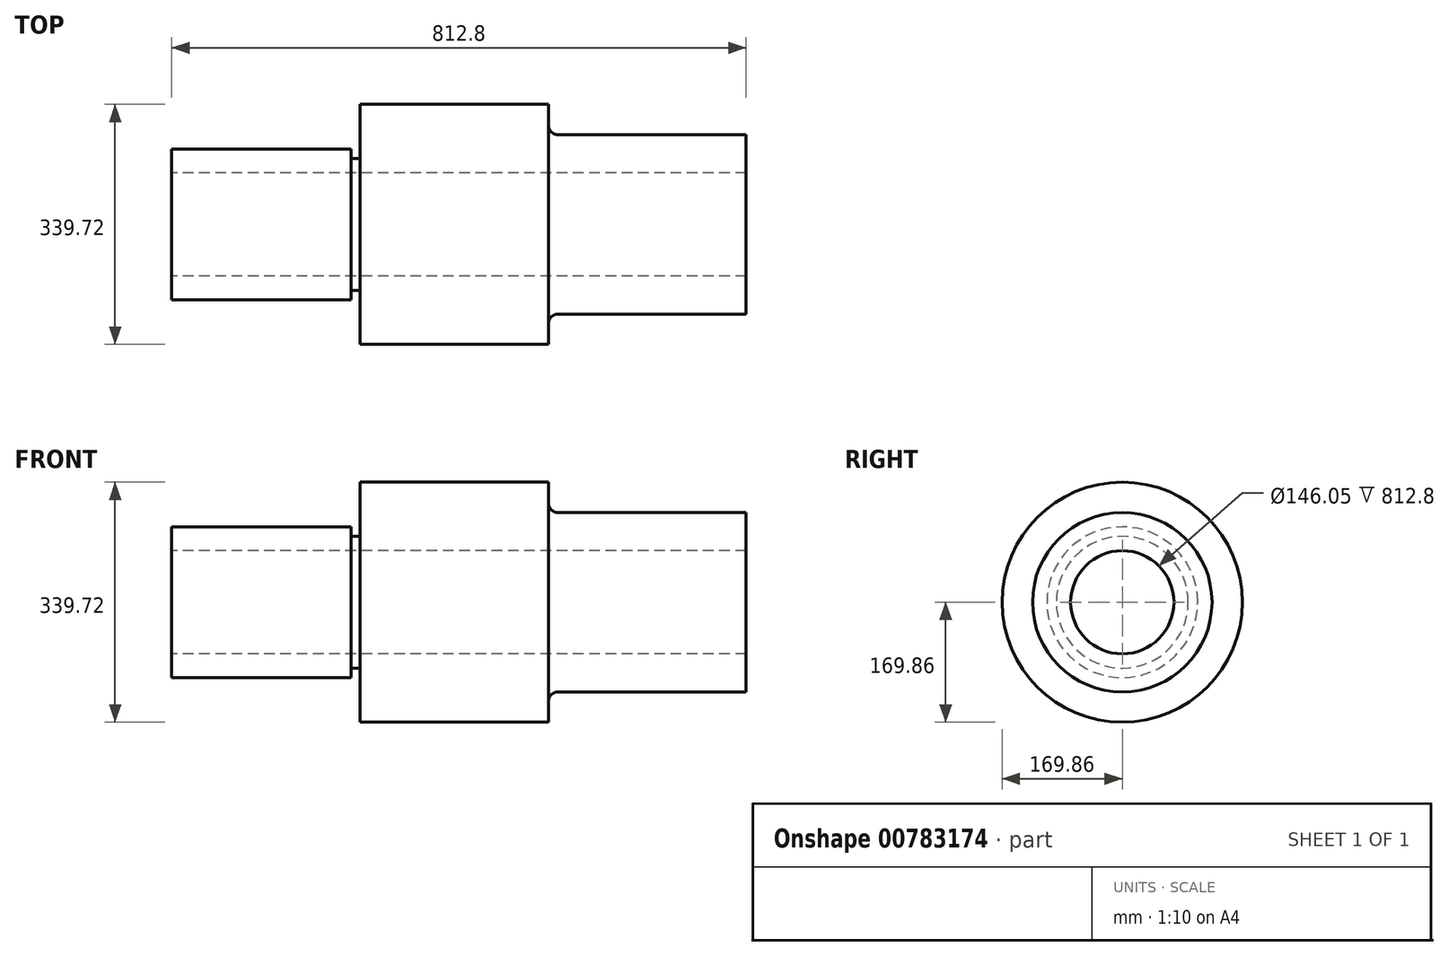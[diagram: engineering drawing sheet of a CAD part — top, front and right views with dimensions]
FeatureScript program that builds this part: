
annotation { "Feature Type Name" : "Feature", "Feature Type Description" : "" }
export const myFeature = defineFeature(function(context is Context, id is Id, definition is map)
    precondition{}
    {
        {
            var Q0;
            Q0=qCreatedBy(makeId("Front.planeOp"),FACE);
            var sketch = newSketch(context, id + "F0", { "sketchPlane" : qUnion([Q0])});
            skLineSegment(sketch, "E0", {"start": v(0, 0) * mm, "end": v(812.8, 0) * mm, "construction": true});
            skLineSegment(sketch, "E1", {"start": v(0, 73.03) * mm, "end": v(0, 106.68) * mm});
            skLineSegment(sketch, "E2", {"start": v(0, 106.68) * mm, "end": v(254, 106.68) * mm});
            skLineSegment(sketch, "E3", {"start": v(266.7, 169.86) * mm, "end": v(533.4, 169.86) * mm});
            skLineSegment(sketch, "E4", {"start": v(533.4, 169.86) * mm, "end": v(533.4, 139.7) * mm});
            skLineSegment(sketch, "E5", {"start": v(546.1, 127) * mm, "end": v(812.8, 127) * mm});
            skLineSegment(sketch, "E6", {"start": v(0, 73.03) * mm, "end": v(812.8, 73.03) * mm});
            skLineSegment(sketch, "E7", {"start": v(812.8, 73.03) * mm, "end": v(812.8, 127) * mm});
            skPoint(sketch, "E8.visualSharp", {"position": v(266.7, 106.68) * mm});
            skPoint(sketch, "E9.visualSharp", {"position": v(533.4, 127) * mm});
            skArc(sketch, "E9.filletArc", {"start": v(533.4, 139.7) * mm, "mid": v(537.12, 130.72) * mm, "end": v(546.1, 127) * mm});
            skLineSegment(sketch, "E10", {"start": v(266.7, 93.28) * mm, "end": v(254, 93.28) * mm});
            skLineSegment(sketch, "E11", {"start": v(254, 93.28) * mm, "end": v(254, 106.68) * mm});
            skPoint(sketch, "E8.filletArc.center.orphan", {"position": v(254, 119.38) * mm});
            skLineSegment(sketch, "E12", {"start": v(266.7, 169.86) * mm, "end": v(266.7, 93.28) * mm});
            skSolve(sketch);
        }
        {
            var Q0;
            Q0 = qSketchRegion(id + "F0", true);
            var Q1;
            Q1=sQuery(id+"F0.wireOp",EDGE,"E0");
            revolve(context, id + "F1", {"surfaceOperationType" : NewSurfaceOperationType.NEW, "entities" : qUnion([Q0]), "axis" : qUnion([Q1]), "revolveType" : RevolveType.FULL});
        }
    });
